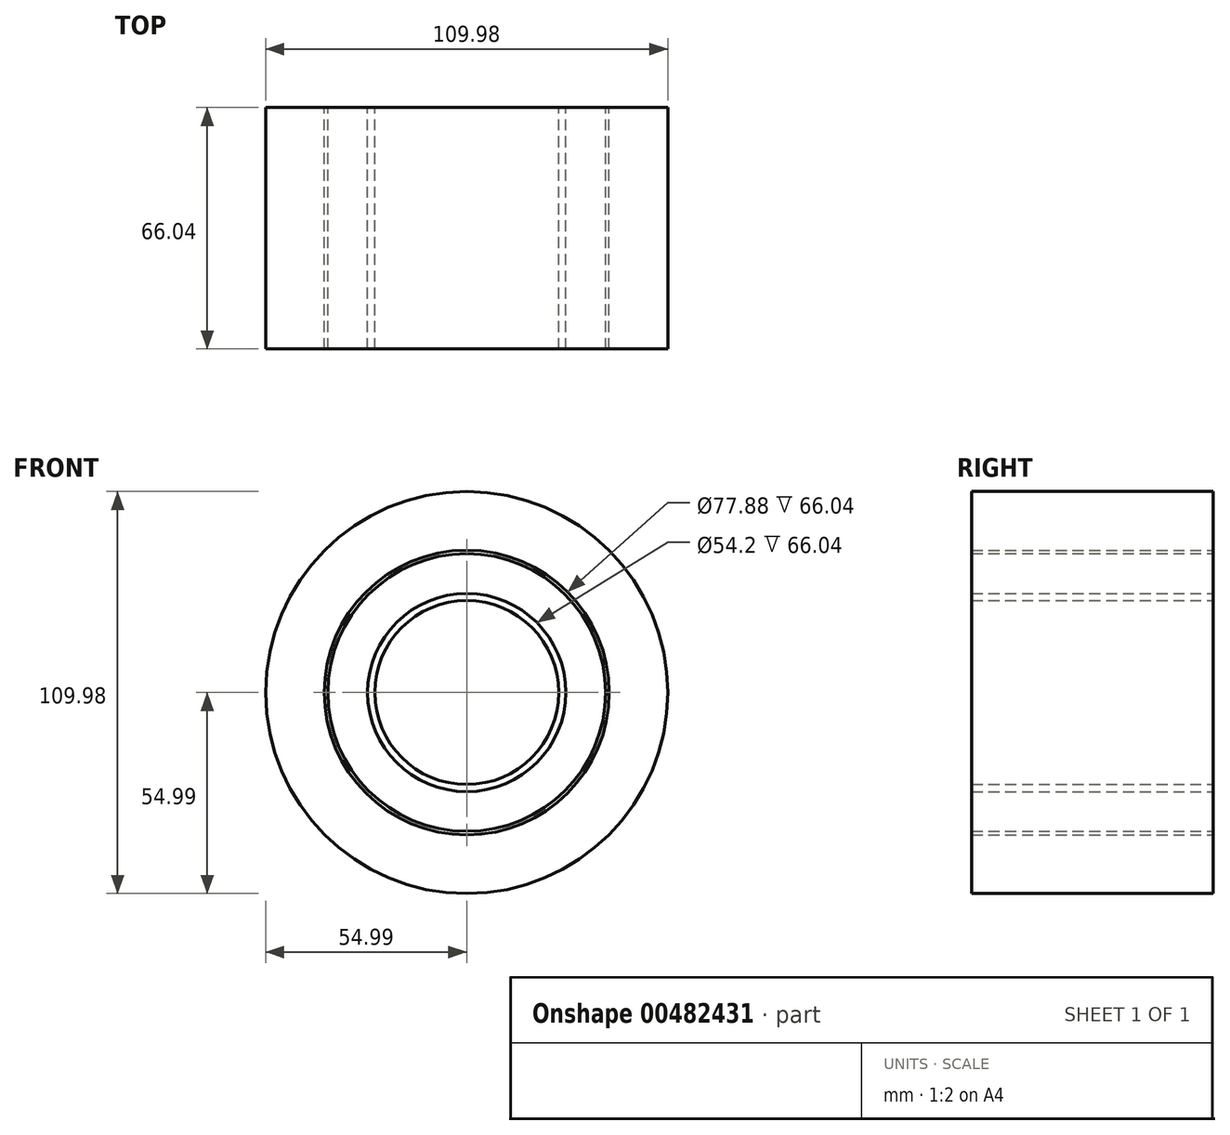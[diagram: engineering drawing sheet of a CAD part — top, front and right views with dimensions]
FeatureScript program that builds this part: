
annotation { "Feature Type Name" : "Feature", "Feature Type Description" : "" }
export const myFeature = defineFeature(function(context is Context, id is Id, definition is map)
    precondition{}
    {
        {
            var Q0;
            Q0=qCreatedBy(makeId("Front.planeOp"),FACE);
            var sketch = newSketch(context, id + "F0", { "sketchPlane" : qUnion([Q0])});
            skCircle(sketch, "E0", {"center": v(0, 0) * mm, "radius": 54.99 * mm});
            skCircle(sketch, "E1", {"center": v(0, 0) * mm, "radius": 38.94 * mm});
            skCircle(sketch, "E2", {"center": v(0, 0) * mm, "radius": 37.98 * mm});
            skCircle(sketch, "E3", {"center": v(0, 0) * mm, "radius": 27.1 * mm});
            skCircle(sketch, "E4", {"center": v(0, 0) * mm, "radius": 25.15 * mm});
            skSolve(sketch);
        }
        {
            var Q0;
            Q0 = qSketchRegion(id + "F0", true);
            var Q1;
            Q1=makeQuery(id+"F0.imprint","IMPRINT",FACE,{"disambiguationData":[TD([[makeQuery(id+"F0.imprint","IMPRINT",EDGE,{"derivedFrom":sQuery(id+"F0.wireOp",EDGE,"E2")}),1.0]])]});
            var Q2;
            Q2=makeQuery(id+"F0.imprint","IMPRINT",FACE,{"disambiguationData":[TD([[makeQuery(id+"F0.imprint","IMPRINT",EDGE,{"derivedFrom":sQuery(id+"F0.wireOp",EDGE,"E4")}),1.0]])]});
            extrude(context, id + "F1", {"entities" : qUnion([Q0, Q1, Q2]), "depth" : 66.04 * mm});
        }
    });
